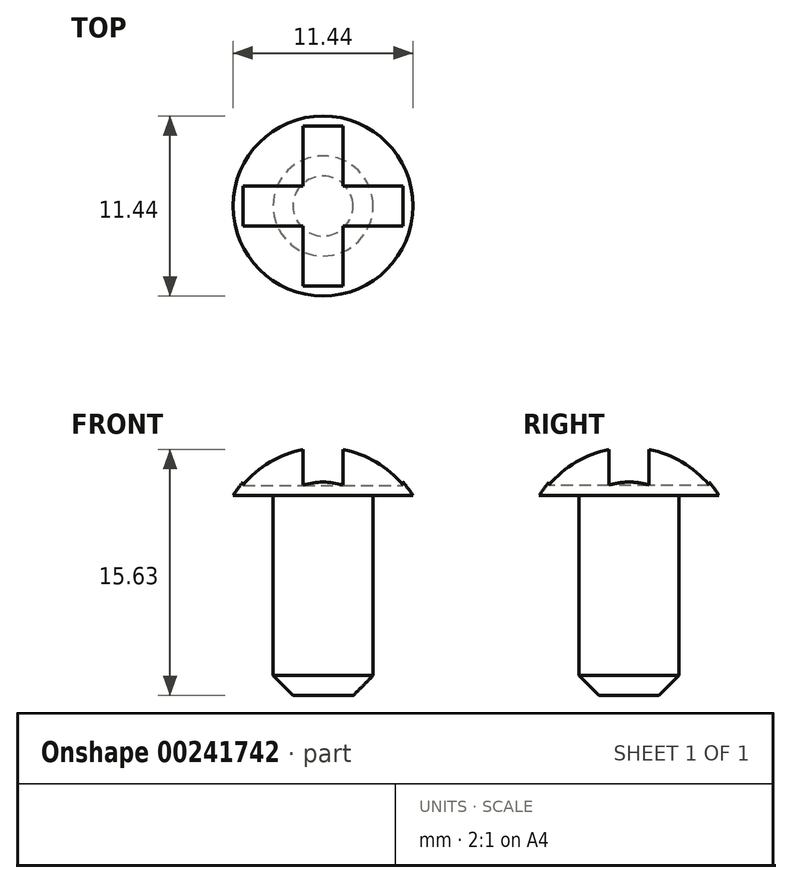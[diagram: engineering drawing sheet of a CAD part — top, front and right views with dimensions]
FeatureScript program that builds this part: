
annotation { "Feature Type Name" : "Feature", "Feature Type Description" : "" }
export const myFeature = defineFeature(function(context is Context, id is Id, definition is map)
    precondition{}
    {
        {
            var Q0;
            Q0=qCreatedBy(makeId("Front.planeOp"),FACE);
            var sketch = newSketch(context, id + "F0", { "sketchPlane" : qUnion([Q0])});
            skLineSegment(sketch, "E0", {"start": v(0, 0) * mm, "end": v(0, 0) * mm});
            skLineSegment(sketch, "E1", {"start": v(0, 0) * mm, "end": v(3.17, 0) * mm});
            skLineSegment(sketch, "E2", {"start": v(3.17, 0) * mm, "end": v(3.17, 12.7) * mm});
            skLineSegment(sketch, "E3", {"start": v(3.17, 12.7) * mm, "end": v(5.72, 12.7) * mm});
            skLineSegment(sketch, "E4", {"start": v(0, 15.88) * mm, "end": v(0, 0) * mm});
            skArc(sketch, "E5", {"start": v(0, 15.88) * mm, "mid": v(3.27, 15.03) * mm, "end": v(5.72, 12.7) * mm});
            skSolve(sketch);
        }
        {
            var Q0;
            Q0=makeQuery(id+"F0.imprint","IMPRINT",FACE,{"disambiguationData":[TD([[makeQuery(id+"F0.imprint","IMPRINT",EDGE,{"derivedFrom":sQuery(id+"F0.wireOp",EDGE,"E1")}),1.0]])]});
            var Q1;
            Q1=sQuery(id+"F0.wireOp",EDGE,"E4");
            revolve(context, id + "F1", {"entities" : qUnion([Q0]), "axis" : qUnion([Q1]), "revolveType" : RevolveType.FULL});
        }
        {
            var Q0;
            Q0=makeQuery(id+"F1.opRevolve","SWEPT_FACE",FACE,{"disambiguationData":[OSD([sQuery(id+"F0.wireOp",EDGE,"E3")])]});
            cPlane(context, id + "F2", {"entities" : qUnion([Q0]), "cplaneType" : CPlaneType.OFFSET, "offset" : 0.64 * mm, "oppositeDirection" : true, "width" : 152.4 * mm, "height" : 152.4 * mm});
        }
        {
            var Q0;
            Q0=qCreatedBy(id+"F2.planeOp",FACE);
            var sketch = newSketch(context, id + "F3", { "sketchPlane" : qUnion([Q0])});
            skLineSegment(sketch, "E6.bottom", {"start": v(-5.08, -1.27) * mm, "end": v(5.08, -1.27) * mm});
            skLineSegment(sketch, "E6.top", {"start": v(-5.08, 1.27) * mm, "end": v(5.08, 1.27) * mm});
            skLineSegment(sketch, "E6.left", {"start": v(-5.08, -1.27) * mm, "end": v(-5.08, 1.27) * mm});
            skLineSegment(sketch, "E6.right", {"start": v(5.08, -1.27) * mm, "end": v(5.08, 1.27) * mm});
            skPoint(sketch, "E6.middle", {"position": v(0, 0) * mm});
            skLineSegment(sketch, "E7.bottom", {"start": v(-1.27, -5.08) * mm, "end": v(1.27, -5.08) * mm});
            skLineSegment(sketch, "E7.top", {"start": v(-1.27, 5.08) * mm, "end": v(1.27, 5.08) * mm});
            skLineSegment(sketch, "E7.left", {"start": v(-1.27, -5.08) * mm, "end": v(-1.27, 5.08) * mm});
            skLineSegment(sketch, "E7.right", {"start": v(1.27, -5.08) * mm, "end": v(1.27, 5.08) * mm});
            skSolve(sketch);
        }
        {
            var Q0;
            Q0=qSketchRegion(id+"F3",true);
            extrude(context, id + "F4", {"entities" : qUnion([Q0]), "operationType" : NewBodyOperationType.REMOVE, "oppositeDirection" : true, "depth" : 6.15 * mm});
        }
        {
            var Q0;
            Q0=makeQuery(id+"F1.opRevolve","SWEPT_FACE",FACE,{"disambiguationData":[OSD([sQuery(id+"F0.wireOp",EDGE,"E1")])]});
            chamfer(context, id + "F5", {"entities" : qUnion([Q0]), "width" : 1.27 * mm, "tangentPropagation" : true});
        }
    });
